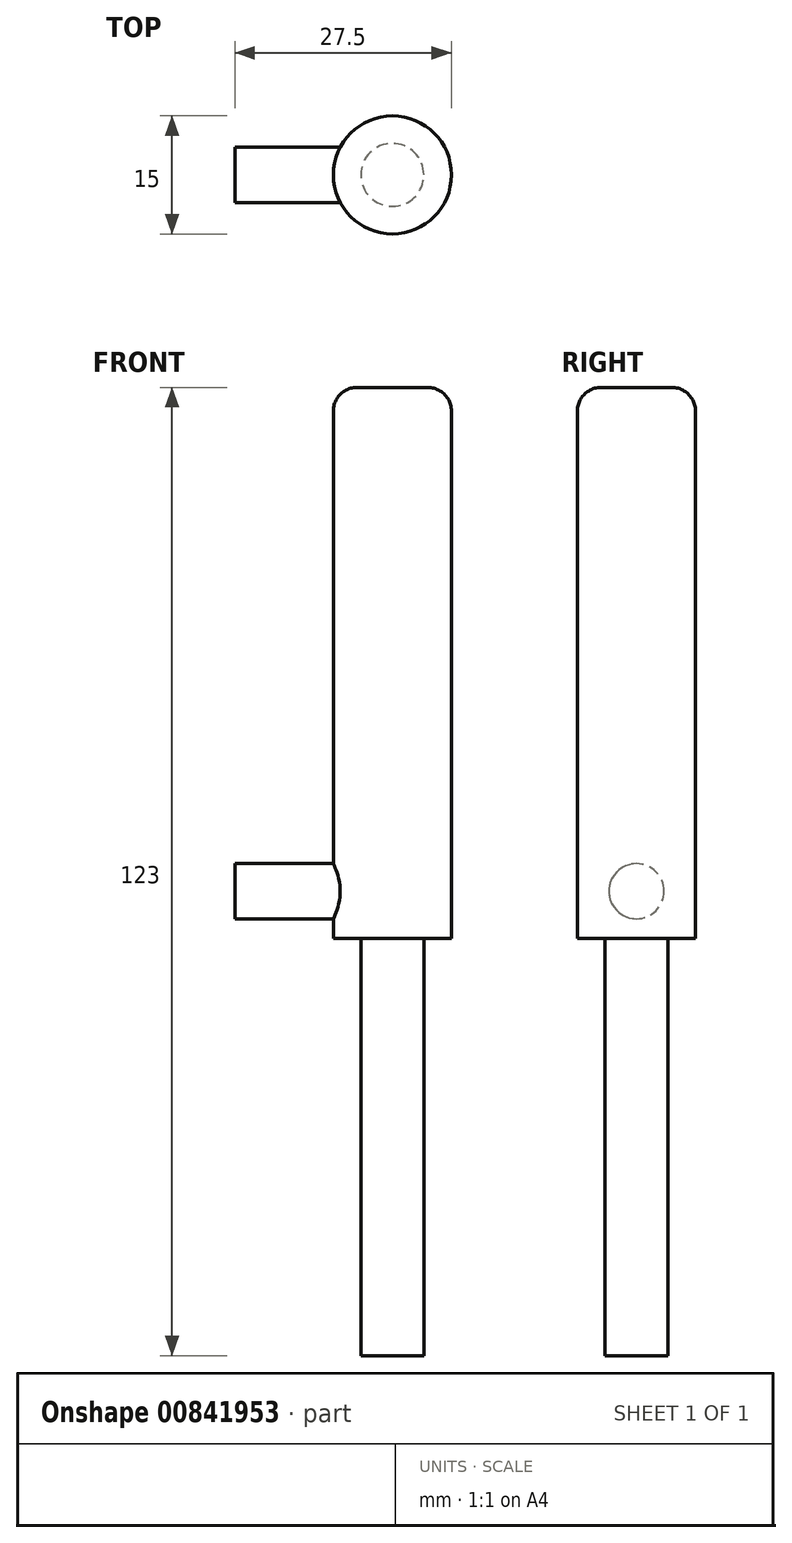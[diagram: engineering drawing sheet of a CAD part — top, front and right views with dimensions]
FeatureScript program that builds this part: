
annotation { "Feature Type Name" : "Feature", "Feature Type Description" : "" }
export const myFeature = defineFeature(function(context is Context, id is Id, definition is map)
    precondition{}
    {
        {
            var Q0;
            Q0=qCreatedBy(makeId("Top.planeOp"),FACE);
            var sketch = newSketch(context, id + "F0", { "sketchPlane" : qUnion([Q0])});
            skCircle(sketch, "E0", {"center": v(0, 0) * mm, "radius": 7.5 * mm});
            skSolve(sketch);
        }
        {
            var Q0;
            Q0 = qSketchRegion(id + "F0", true);
            extrude(context, id + "F1", {"entities" : qUnion([Q0]), "depth" : 100 * mm, "offsetDistance" : 25 * mm});
        }
        {
            var Q0;
            Q0=makeQuery(id+"F1.opExtrude","CAP_EDGE",EDGE,{"disambiguationData":[OSD([sQuery(id+"F0.wireOp",EDGE,"E0")])],"isStart":false});
            fillet(context, id + "F2", {"entities" : qUnion([Q0]), "radius" : 3 * mm, "tangentPropagation" : true, "allowEdgeOverflow" : false});
        }
        {
            var Q0;
            Q0=makeQuery(id+"F1.opExtrude","CAP_FACE",FACE,{"disambiguationData":[OSD([sQuery(id+"F0.wireOp",EDGE,"E0")])],"isStart":true});
            var sketch = newSketch(context, id + "F3", { "sketchPlane" : qUnion([Q0])});
            skCircle(sketch, "E1", {"center": v(0, 0) * mm, "radius": 4 * mm});
            skSolve(sketch);
        }
        {
            var Q0;
            Q0=makeQuery(id+"F3.imprint","IMPRINT",FACE,{"disambiguationData":[TD([[makeQuery(id+"F3.imprint","IMPRINT",EDGE,{"derivedFrom":sQuery(id+"F3.wireOp",EDGE,"E1")}),-1.0]])]});
            extrude(context, id + "F4", {"entities" : qUnion([Q0]), "operationType" : NewBodyOperationType.REMOVE, "oppositeDirection" : true, "depth" : 30 * mm, "offsetDistance" : 25 * mm});
        }
        {
            var Q0;
            Q0=qCreatedBy(makeId("Right.planeOp"),FACE);
            var sketch = newSketch(context, id + "F5", { "sketchPlane" : qUnion([Q0])});
            skCircle(sketch, "E2", {"center": v(0, 36) * mm, "radius": 3.5 * mm});
            skSolve(sketch);
        }
        {
            var Q0;
            Q0 = qSketchRegion(id + "F5", true);
            extrude(context, id + "F6", {"entities" : qUnion([Q0]), "operationType" : NewBodyOperationType.ADD, "oppositeDirection" : true, "depth" : 20 * mm, "offsetDistance" : 25 * mm});
        }
        {
            var Q0;
            Q0=makeQuery(id+"F1.opExtrude","CAP_FACE",FACE,{"disambiguationData":[OSD([sQuery(id+"F0.wireOp",EDGE,"E0")])],"isStart":true});
            extrude(context, id + "F7", {"entities" : qUnion([Q0]), "operationType" : NewBodyOperationType.ADD, "depth" : 23 * mm, "offsetDistance" : 25 * mm});
        }
    });
